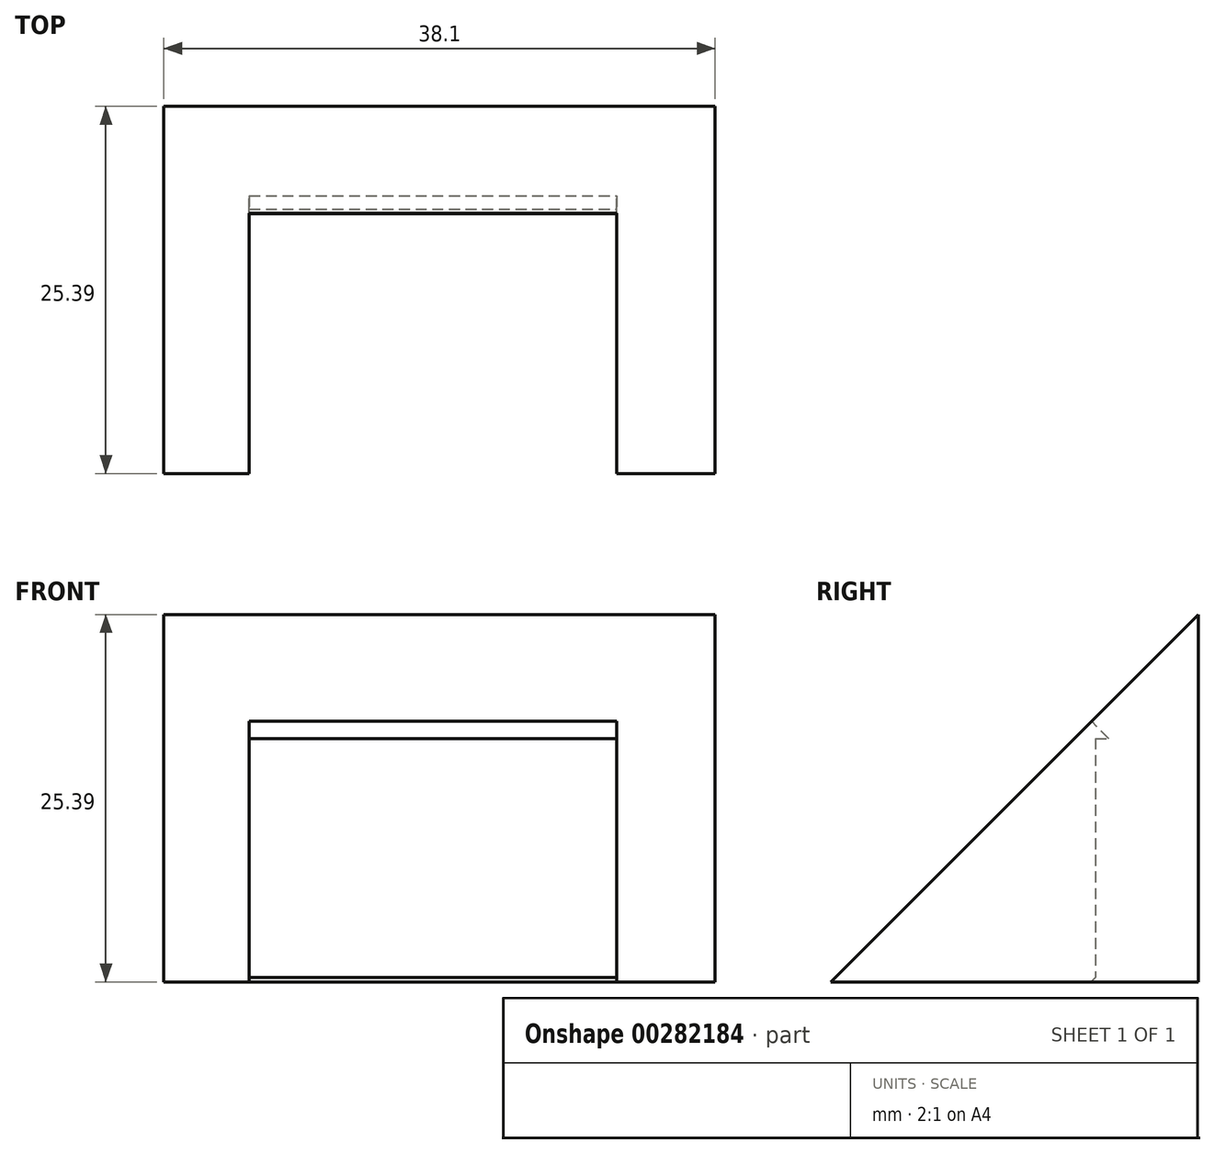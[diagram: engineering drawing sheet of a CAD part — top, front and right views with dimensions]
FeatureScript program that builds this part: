
annotation { "Feature Type Name" : "Feature", "Feature Type Description" : "" }
export const myFeature = defineFeature(function(context is Context, id is Id, definition is map)
    precondition{}
    {
        {
            var Q0;
            Q0=qCreatedBy(makeId("Right.planeOp"),FACE);
            var sketch = newSketch(context, id + "F0", { "sketchPlane" : qUnion([Q0])});
            skLineSegment(sketch, "E0", {"start": v(0, 0) * mm, "end": v(0, 25.4) * mm});
            skLineSegment(sketch, "E1", {"start": v(0, 0) * mm, "end": v(-25.4, 0) * mm});
            skLineSegment(sketch, "E2", {"start": v(-25.4, 0) * mm, "end": v(0, 25.4) * mm});
            skSolve(sketch);
        }
        {
            var Q0;
            Q0 = qSketchRegion(id + "F0", true);
            extrude(context, id + "F1", {"entities" : qUnion([Q0]), "depth" : 38.1 * mm});
        }
        {
            var Q0;
            Q0=makeQuery(id+"F1.opExtrude","SWEPT_FACE",FACE,{"disambiguationData":[OSD([sQuery(id+"F0.wireOp",EDGE,"E2")])]});
            var sketch = newSketch(context, id + "F2", { "sketchPlane" : qUnion([Q0])});
            skLineSegment(sketch, "E3.bottom", {"start": v(5.9, -17.95) * mm, "end": v(31.3, -17.95) * mm});
            skLineSegment(sketch, "E3.top", {"start": v(5.9, 7.52) * mm, "end": v(31.3, 7.52) * mm});
            skLineSegment(sketch, "E3.left", {"start": v(5.9, -17.95) * mm, "end": v(5.9, 7.52) * mm});
            skLineSegment(sketch, "E3.right", {"start": v(31.3, -17.95) * mm, "end": v(31.3, 7.52) * mm});
            skSolve(sketch);
        }
        {
            var Q0;
            Q0 = qSketchRegion(id + "F2", true);
            extrude(context, id + "F3", {"entities" : qUnion([Q0]), "operationType" : NewBodyOperationType.REMOVE, "endBound" : BoundingType.SYMMETRIC, "oppositeDirection" : true, "depth" : 25.4 * mm});
        }
        {
            var Q0;
            Q0=qCreatedBy(makeId("Front.planeOp"),FACE);
            var sketch = newSketch(context, id + "F4", { "sketchPlane" : qUnion([Q0])});
            skLineSegment(sketch, "E4.bottom", {"start": v(31.89, 16.83) * mm, "end": v(5.9, 16.83) * mm});
            skLineSegment(sketch, "E4.top", {"start": v(31.89, 0) * mm, "end": v(5.9, 0) * mm});
            skLineSegment(sketch, "E4.left", {"start": v(31.89, 16.83) * mm, "end": v(31.89, 0) * mm});
            skLineSegment(sketch, "E4.right", {"start": v(5.9, 16.83) * mm, "end": v(5.9, 0) * mm});
            skLineSegment(sketch, "E5.left", {"start": v(31.89, 0) * mm, "end": v(31.89, 0) * mm});
            skLineSegment(sketch, "E5.right", {"start": v(5.9, 0) * mm, "end": v(5.9, 0) * mm});
            skSolve(sketch);
        }
        {
            var Q0;
            Q0 = qSketchRegion(id + "F4", true);
            extrude(context, id + "F5", {"entities" : qUnion([Q0]), "operationType" : NewBodyOperationType.ADD, "depth" : 7.11 * mm});
        }
    });
